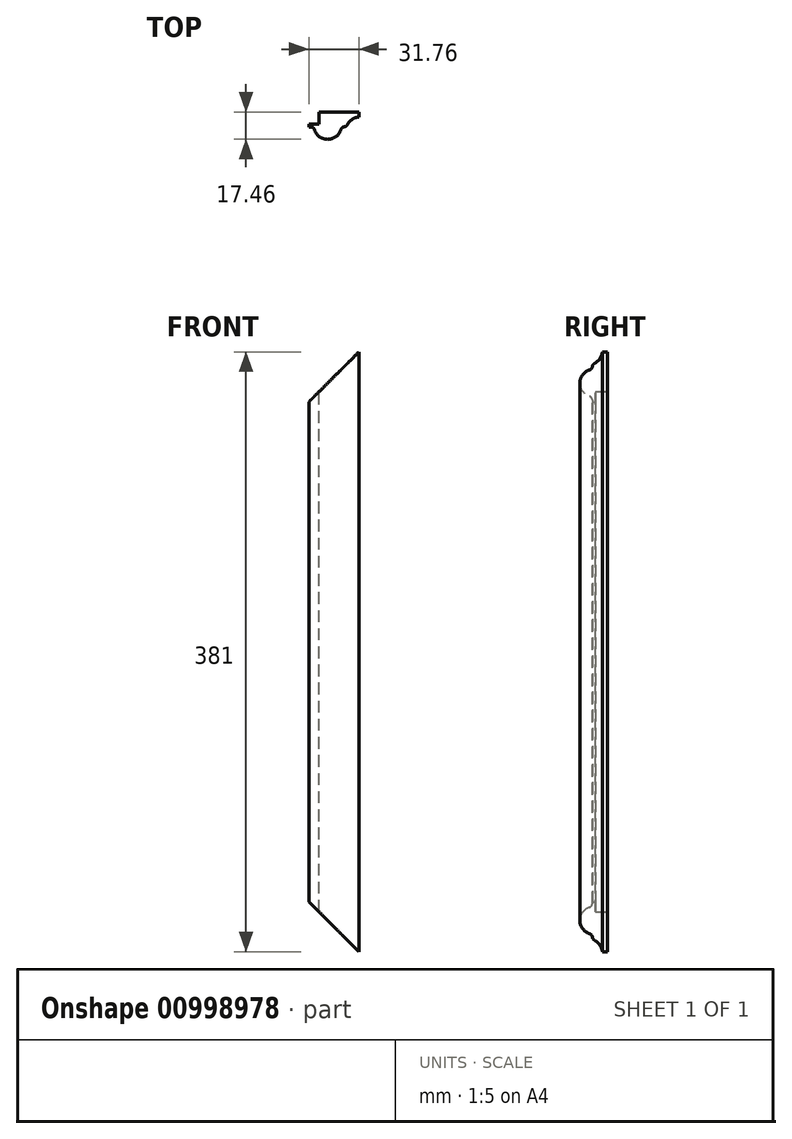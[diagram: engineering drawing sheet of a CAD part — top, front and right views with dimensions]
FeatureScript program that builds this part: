
annotation { "Feature Type Name" : "Feature", "Feature Type Description" : "" }
export const myFeature = defineFeature(function(context is Context, id is Id, definition is map)
    precondition{}
    {
        {
            var Q0;
            Q0=qCreatedBy(makeId("Top.planeOp"),FACE);
            var sketch = newSketch(context, id + "F0", { "sketchPlane" : qUnion([Q0])});
            skLineSegment(sketch, "E0.bottom", {"start": v(15.88, 8.73) * mm, "end": v(-15.88, 8.73) * mm});
            skLineSegment(sketch, "E0.top", {"start": v(-3.97, -8.73) * mm, "end": v(-3.98, -8.73) * mm});
            skLineSegment(sketch, "E0.left", {"start": v(15.88, 8.73) * mm, "end": v(15.88, -0.8) * mm});
            skLineSegment(sketch, "E0.right", {"start": v(-15.88, 8.73) * mm, "end": v(-15.88, -0.8) * mm});
            skPoint(sketch, "E0.middle", {"position": v(0, 0) * mm});
            skLineSegment(sketch, "E1", {"start": v(15.88, 8.73) * mm, "end": v(15.88, 5.56) * mm});
            skLineSegment(sketch, "E2", {"start": v(-19.4, -0.8) * mm, "end": v(24.15, -0.8) * mm, "construction": true});
            skLineSegment(sketch, "E3", {"start": v(21.72, 5.56) * mm, "end": v(-20.21, 5.56) * mm, "construction": true});
            skPoint(sketch, "E4", {"position": v(7.94, -0.8) * mm});
            skPoint(sketch, "E5", {"position": v(4.76, -0.8) * mm});
            skPoint(sketch, "E6", {"position": v(-12.7, -0.8) * mm});
            skLineSegment(sketch, "E7", {"start": v(-15.88, -0.8) * mm, "end": v(-12.7, -0.8) * mm});
            skLineSegment(sketch, "E8", {"start": v(4.76, -0.8) * mm, "end": v(7.94, -0.8) * mm});
            skPoint(sketch, "E9", {"position": v(-3.98, -8.73) * mm});
            skArc(sketch, "E10", {"start": v(15.88, 5.56) * mm, "mid": v(10.99, 3.53) * mm, "end": v(7.94, -0.8) * mm});
            skArc(sketch, "E11", {"start": v(-12.7, -0.8) * mm, "mid": v(-3.97, -8.73) * mm, "end": v(4.76, -0.8) * mm});
            skPoint(sketch, "E12.orphan", {"position": v(-15.88, -8.73) * mm});
            skPoint(sketch, "E13.orphan", {"position": v(15.88, -8.73) * mm});
            skSolve(sketch);
        }
        {
            var Q0;
            Q0=makeQuery(id+"F0.imprint","IMPRINT",FACE,{"disambiguationData":[TD([[makeQuery(id+"F0.imprint","IMPRINT",EDGE,{"derivedFrom":sQuery(id+"F0.wireOp",EDGE,"E0.bottom")}),1.0]])]});
            extrude(context, id + "F1", {"entities" : qUnion([Q0]), "depth" : 381 * mm, "offsetDistance" : 25.4 * mm});
        }
        {
            var Q0;
            Q0=makeQuery(id+"F1.opExtrude","SWEPT_EDGE",EDGE,{"disambiguationData":[OSD([sQuery(id+"F0.wireOp",EDGE,"E8"),sQuery(id+"F0.wireOp",EDGE,"E10")])]});
            fillet(context, id + "F2", {"entities" : qUnion([Q0]), "radius" : 2.54 * mm, "tangentPropagation" : true, "allowEdgeOverflow" : false});
        }
        {
            var Q0;
            Q0=makeQuery(id+"F1.opExtrude","SWEPT_EDGE",EDGE,{"disambiguationData":[OSD([sQuery(id+"F0.wireOp",EDGE,"E7"),sQuery(id+"F0.wireOp",EDGE,"E11")])]});
            fillet(context, id + "F3", {"entities" : qUnion([Q0]), "radius" : 2.54 * mm, "tangentPropagation" : true, "allowEdgeOverflow" : false});
        }
        {
            var Q0;
            Q0=makeQuery(id+"F1.opExtrude","SWEPT_EDGE",EDGE,{"disambiguationData":[OSD([sQuery(id+"F0.wireOp",EDGE,"E8"),sQuery(id+"F0.wireOp",EDGE,"E11")])]});
            fillet(context, id + "F4", {"entities" : qUnion([Q0]), "radius" : 2.54 * mm, "tangentPropagation" : true, "allowEdgeOverflow" : false});
        }
        {
            var Q0;
            Q0=makeQuery(id+"FtKLiYXaFetn44W_1.boolean.opBoolean","SPLIT",FACE,{"disambiguationData":[TD([makeQuery(id+"FtKLiYXaFetn44W_1.opExtrude","SWEPT_FACE",FACE,{"disambiguationData":[OSD([sQuery(id+"FxCuGDugNnE8EV2_1.wireOp",EDGE,"FmI5fHck-0ub2-xswP-vLsR-ZfJuQmsgoC2R")])]})])],"derivedFrom":makeQuery(id+"F1.opExtrude","SWEPT_FACE",FACE,{"disambiguationData":[OSD([sQuery(id+"F0.wireOp",EDGE,"E0.bottom")])]})});
            var sketch = newSketch(context, id + "F5", { "sketchPlane" : qUnion([Q0])});
            skLineSegment(sketch, "E14.bottom", {"start": v(15.88, 0) * mm, "end": v(9.52, 0) * mm});
            skLineSegment(sketch, "E14.top", {"start": v(15.87, 381) * mm, "end": v(9.52, 381) * mm});
            skLineSegment(sketch, "E14.left", {"start": v(15.88, 0) * mm, "end": v(15.87, 381) * mm});
            skLineSegment(sketch, "E14.right", {"start": v(9.52, 0) * mm, "end": v(9.52, 381) * mm});
            skSolve(sketch);
        }
        {
            var Q0;
            Q0 = qSketchRegion(id + "F5", true);
            extrude(context, id + "F6", {"entities" : qUnion([Q0]), "operationType" : NewBodyOperationType.REMOVE, "oppositeDirection" : true, "depth" : 7.62 * mm, "offsetDistance" : 25.4 * mm});
        }
        {
            var Q0;
            Q0=makeQuery(id+"F1.opExtrude","SWEPT_FACE",FACE,{"disambiguationData":[OSD([sQuery(id+"F0.wireOp",EDGE,"E0.bottom")])]});
            var sketch = newSketch(context, id + "F7", { "sketchPlane" : qUnion([Q0])});
            skLineSegment(sketch, "E15", {"start": v(15.88, 31.75) * mm, "end": v(-15.88, 0) * mm});
            skLineSegment(sketch, "E16", {"start": v(-15.88, 0) * mm, "end": v(15.88, 0) * mm});
            skLineSegment(sketch, "E17.MirrorCS", {"start": v(15.87, 0) * mm, "end": v(15.87, 31.75) * mm});
            skLineSegment(sketch, "E18", {"start": v(-15.88, 381) * mm, "end": v(15.87, 381) * mm});
            skLineSegment(sketch, "E19", {"start": v(-15.88, 381) * mm, "end": v(15.87, 349.25) * mm});
            skLineSegment(sketch, "E20", {"start": v(15.88, 349.25) * mm, "end": v(15.88, 381) * mm});
            skSolve(sketch);
        }
        {
            var Q0;
            Q0 = qSketchRegion(id + "F7", true);
            extrude(context, id + "F8", {"entities" : qUnion([Q0]), "operationType" : NewBodyOperationType.REMOVE, "endBound" : BoundingType.THROUGH_ALL, "oppositeDirection" : true, "depth" : 25.4 * mm, "offsetDistance" : 25.4 * mm});
        }
    });
